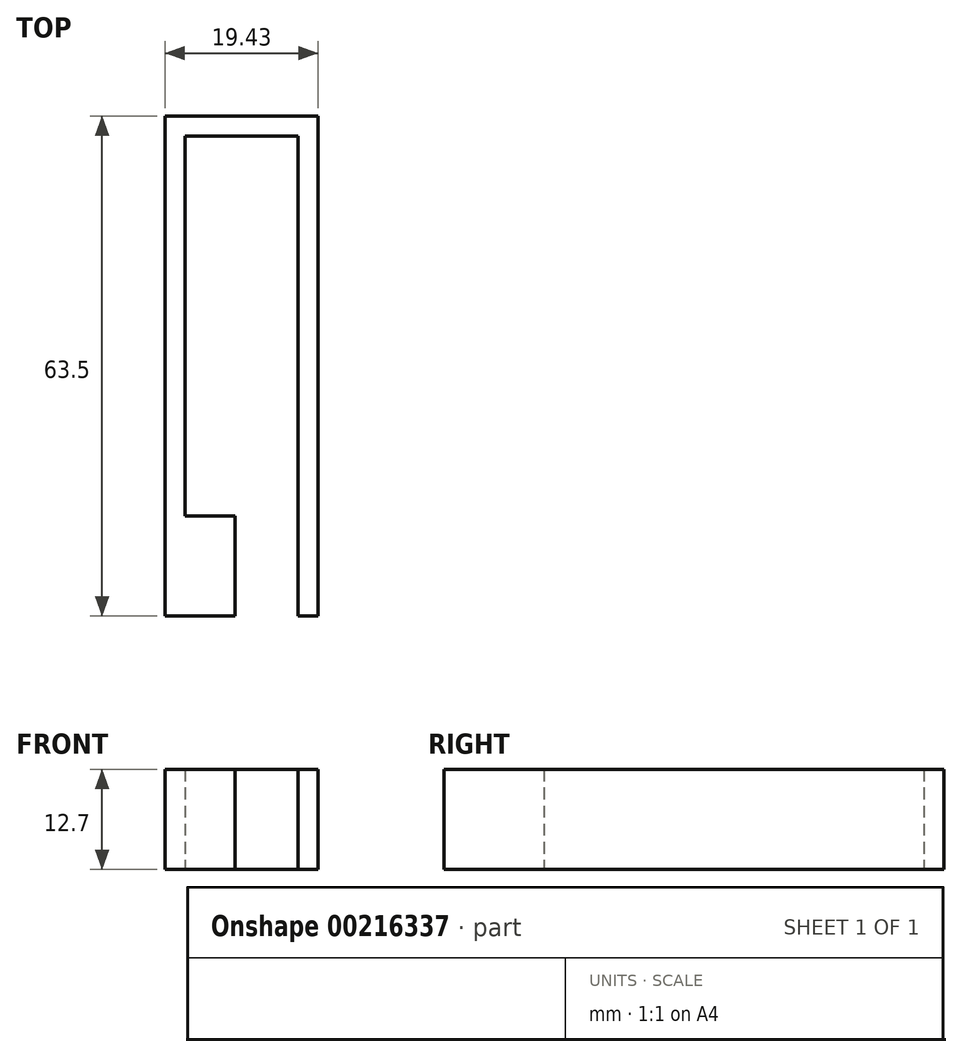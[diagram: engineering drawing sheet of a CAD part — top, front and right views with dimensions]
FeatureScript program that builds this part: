
annotation { "Feature Type Name" : "Feature", "Feature Type Description" : "" }
export const myFeature = defineFeature(function(context is Context, id is Id, definition is map)
    precondition{}
    {
        {
            var Q0;
            Q0=qCreatedBy(makeId("Top.planeOp"),FACE);
            var sketch = newSketch(context, id + "F0", { "sketchPlane" : qUnion([Q0])});
            skLineSegment(sketch, "E0.bottom", {"start": v(1.27, -31.75) * mm, "end": v(-1.27, -31.75) * mm});
            skLineSegment(sketch, "E0.top", {"start": v(1.27, 31.75) * mm, "end": v(-1.27, 31.75) * mm});
            skLineSegment(sketch, "E0.left", {"start": v(1.27, -31.75) * mm, "end": v(1.27, 31.75) * mm});
            skLineSegment(sketch, "E0.right", {"start": v(-1.27, -31.75) * mm, "end": v(-1.27, 31.75) * mm});
            skPoint(sketch, "E0.middle", {"position": v(0, 0) * mm});
            skLineSegment(sketch, "E1.bottom", {"start": v(-1.27, 31.75) * mm, "end": v(-15.62, 31.75) * mm});
            skLineSegment(sketch, "E1.top", {"start": v(-1.27, 29.21) * mm, "end": v(-15.62, 29.21) * mm});
            skLineSegment(sketch, "E1.left", {"start": v(-1.27, 31.75) * mm, "end": v(-1.27, 29.21) * mm});
            skLineSegment(sketch, "E1.right", {"start": v(-15.62, 31.75) * mm, "end": v(-15.62, 29.21) * mm});
            skLineSegment(sketch, "E2.bottom", {"start": v(-15.62, 31.75) * mm, "end": v(-18.16, 31.75) * mm});
            skLineSegment(sketch, "E2.top", {"start": v(-15.62, -31.75) * mm, "end": v(-18.16, -31.75) * mm});
            skLineSegment(sketch, "E2.left", {"start": v(-15.62, 31.75) * mm, "end": v(-15.62, -31.75) * mm});
            skLineSegment(sketch, "E2.right", {"start": v(-18.16, 31.75) * mm, "end": v(-18.16, -31.75) * mm});
            skLineSegment(sketch, "E3.bottom", {"start": v(-15.62, -31.75) * mm, "end": v(-9.27, -31.75) * mm});
            skLineSegment(sketch, "E3.top", {"start": v(-15.62, -19.05) * mm, "end": v(-9.27, -19.05) * mm});
            skLineSegment(sketch, "E3.left", {"start": v(-15.62, -31.75) * mm, "end": v(-15.62, -19.05) * mm});
            skLineSegment(sketch, "E3.right", {"start": v(-9.27, -31.75) * mm, "end": v(-9.27, -19.05) * mm});
            skSolve(sketch);
        }
        {
            var Q0;
            Q0=makeQuery(id+"F0.imprint","IMPRINT",FACE,{"disambiguationData":[TD([[makeQuery(id+"F0.imprint","IMPRINT",EDGE,{"derivedFrom":sQuery(id+"F0.wireOp",EDGE,"E3.bottom")}),1.0]])]});
            var Q1;
            {var subQ3=sQuery(id+"F0.wireOp",EDGE,"E2.bottom");Q1=makeQuery(id+"F0.imprint","IMPRINT",FACE,{"disambiguationData":[TD([[makeQuery(id+"F0.imprint","IMPRINT",EDGE,{"derivedFrom":subQ3}),1.0]])]});}
            var Q2;
            {var subQ0=sQuery(id+"F0.wireOp",EDGE,"E1.bottom");Q2=makeQuery(id+"F0.imprint","IMPRINT",FACE,{"disambiguationData":[TD([[makeQuery(id+"F0.imprint","IMPRINT",EDGE,{"derivedFrom":subQ0}),1.0]])]});}
            var Q3;
            Q3=makeQuery(id+"F0.imprint","IMPRINT",FACE,{"disambiguationData":[TD([[makeQuery(id+"F0.imprint","IMPRINT",EDGE,{"derivedFrom":sQuery(id+"F0.wireOp",EDGE,"E0.bottom")}),-1.0]])]});
            extrude(context, id + "F1", {"entities" : qUnion([Q0, Q1, Q2, Q3]), "depth" : 12.7 * mm});
        }
    });
